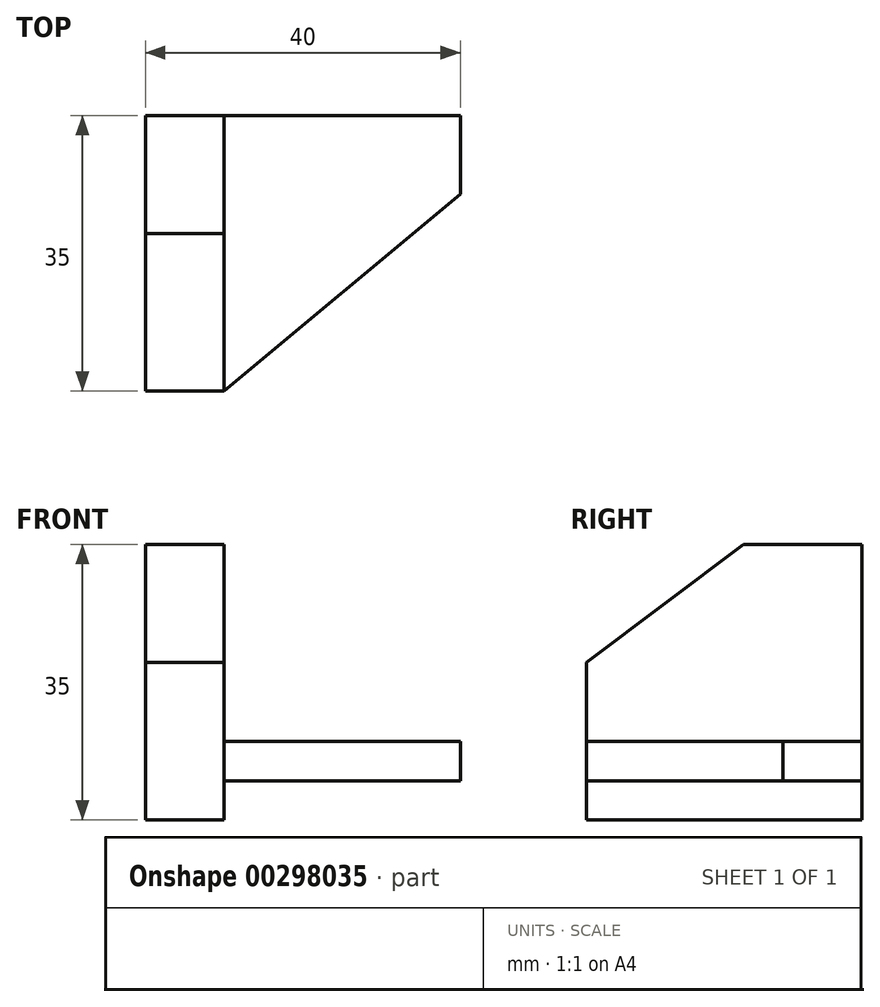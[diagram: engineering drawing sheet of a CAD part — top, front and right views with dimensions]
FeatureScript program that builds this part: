
annotation { "Feature Type Name" : "Feature", "Feature Type Description" : "" }
export const myFeature = defineFeature(function(context is Context, id is Id, definition is map)
    precondition{}
    {
        {
            var Q0;
            Q0=qCreatedBy(makeId("Front.planeOp"),FACE);
            var sketch = newSketch(context, id + "F0", { "sketchPlane" : qUnion([Q0])});
            skLineSegment(sketch, "E0.bottom", {"start": v(32.5, 20) * mm, "end": v(-32.5, 20) * mm});
            skLineSegment(sketch, "E0.top", {"start": v(32.5, -20) * mm, "end": v(-32.5, -20) * mm});
            skLineSegment(sketch, "E0.left", {"start": v(32.5, 20) * mm, "end": v(32.5, -20) * mm});
            skLineSegment(sketch, "E0.right", {"start": v(-32.5, 20) * mm, "end": v(-32.5, -20) * mm});
            skPoint(sketch, "E0.middle", {"position": v(0, 0) * mm});
            skLineSegment(sketch, "E1.top", {"start": v(-32.5, 20) * mm, "end": v(32.5, 20) * mm});
            skLineSegment(sketch, "E1.left", {"start": v(-32.5, 10) * mm, "end": v(-32.5, 20) * mm});
            skLineSegment(sketch, "E1.right", {"start": v(32.5, 10) * mm, "end": v(32.5, 20) * mm});
            skLineSegment(sketch, "E2.bottom", {"start": v(-22.5, 20) * mm, "end": v(-32.5, 20) * mm});
            skLineSegment(sketch, "E2.top", {"start": v(-22.5, -20) * mm, "end": v(-32.5, -20) * mm});
            skLineSegment(sketch, "E3.bottom", {"start": v(-32.5, 15) * mm, "end": v(-22.5, 15) * mm});
            skLineSegment(sketch, "E3.top", {"start": v(-32.5, -20) * mm, "end": v(-22.5, -20) * mm});
            skLineSegment(sketch, "E3.left", {"start": v(-32.5, 15) * mm, "end": v(-32.5, -20) * mm});
            skLineSegment(sketch, "E3.right", {"start": v(-22.5, 15) * mm, "end": v(-22.5, -20) * mm});
            skLineSegment(sketch, "E4", {"start": v(-7.5, 20) * mm, "end": v(32.5, 0) * mm});
            skLineSegment(sketch, "E5.bottom", {"start": v(-22.5, -10) * mm, "end": v(7.5, -10) * mm});
            skLineSegment(sketch, "E5.top", {"start": v(-22.5, -15) * mm, "end": v(7.5, -15) * mm});
            skLineSegment(sketch, "E5.left", {"start": v(-22.5, -10) * mm, "end": v(-22.5, -15) * mm});
            skLineSegment(sketch, "E5.right", {"start": v(7.5, -10) * mm, "end": v(7.5, -15) * mm});
            skSolve(sketch);
        }
        {
            var Q0;
            {var subQ1=sQuery(id+"F0.wireOp",EDGE,"E0.top");Q0=makeQuery(id+"F0.imprint","IMPRINT",FACE,{"disambiguationData":[TD([[makeQuery(id+"F0.imprint","IMPRINT",EDGE,{"derivedFrom":subQ1}),-1.0]])]});}
            extrude(context, id + "F1", {"entities" : qUnion([Q0]), "depth" : 10 * mm});
        }
        {
            var Q0;
            {var subQ1=sQuery(id+"F0.wireOp",EDGE,"E3.bottom");Q0=makeQuery(id+"F0.imprint","IMPRINT",FACE,{"disambiguationData":[TD([[makeQuery(id+"F0.imprint","IMPRINT",EDGE,{"derivedFrom":subQ1}),-1.0]])]});}
            var Q1;
            Q1=makeQuery(id+"F0.imprint","IMPRINT",FACE,{"disambiguationData":[TD([[makeQuery(id+"F0.imprint","IMPRINT",EDGE,{"derivedFrom":sQuery(id+"F0.wireOp",EDGE,"E5.bottom")}),-1.0]])]});
            extrude(context, id + "F2", {"entities" : qUnion([Q0, Q1]), "operationType" : NewBodyOperationType.ADD, "depth" : 35 * mm});
        }
        {
            var Q0;
            Q0=makeQuery(id+"F2.opExtrude","SWEPT_FACE",FACE,{"disambiguationData":[OSD([sQuery(id+"F0.wireOp",EDGE,"E5.bottom")])]});
            var sketch = newSketch(context, id + "F3", { "sketchPlane" : qUnion([Q0])});
            skLineSegment(sketch, "E6", {"start": v(-22.5, -35) * mm, "end": v(7.5, -10) * mm});
            skSolve(sketch);
        }
        {
            var Q0;
            Q0 = qSketchRegion(id + "F3", true);
            var Q1;
            Q1=makeQuery(id+"F3.imprint","IMPRINT",FACE,{"disambiguationData":[TD([[makeQuery(id+"F3.imprint","IMPRINT",EDGE,{"derivedFrom":sQuery(id+"F3.wireOp",EDGE,"E6")}),-1.0]])]});
            extrude(context, id + "F4", {"entities" : qUnion([Q0, Q1]), "operationType" : NewBodyOperationType.REMOVE, "endBound" : BoundingType.THROUGH_ALL, "oppositeDirection" : true, "depth" : 25 * mm});
        }
        {
            var Q0;
            {var subQ0=sQuery(id+"F0.wireOp",EDGE,"E3.right");Q0=makeQuery(id+"F2.opExtrude","SWEPT_FACE",FACE,{"disambiguationData":[OSD([subQ0]),TDD([makeQuery(id+"F0.imprint","IMPRINT",EDGE,{"disambiguationData":[TD([[makeQuery(id+"F0.imprint","INTERSECT",VERTEX,{"derivedFrom":[sQuery(id+"F0.wireOp",EDGE,"E3.bottom"),subQ0]}),-1.0]])],"derivedFrom":subQ0})])]});}
            var sketch = newSketch(context, id + "F5", { "sketchPlane" : qUnion([Q0])});
            skLineSegment(sketch, "E7", {"start": v(-35, 0) * mm, "end": v(-15, 15) * mm});
            skSolve(sketch);
        }
        {
            var Q0;
            {var subQ0=sQuery(id+"F5.wireOp",EDGE,"E7");Q0=makeQuery(id+"F5.imprint","IMPRINT",FACE,{"disambiguationData":[TD([[makeQuery(id+"F5.imprint","IMPRINT",EDGE,{"derivedFrom":subQ0}),1.0]])]});}
            extrude(context, id + "F6", {"entities" : qUnion([Q0]), "operationType" : NewBodyOperationType.REMOVE, "endBound" : BoundingType.THROUGH_ALL, "oppositeDirection" : true, "depth" : 25 * mm});
        }
    });
